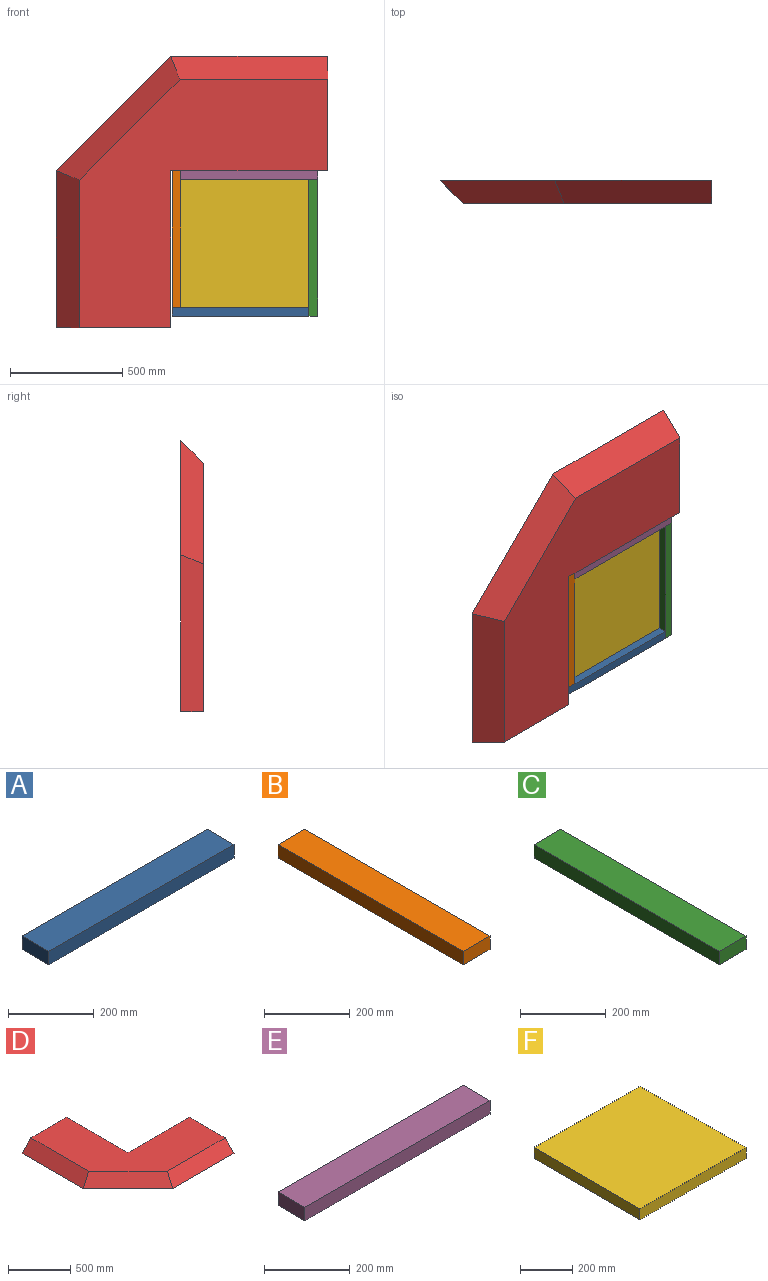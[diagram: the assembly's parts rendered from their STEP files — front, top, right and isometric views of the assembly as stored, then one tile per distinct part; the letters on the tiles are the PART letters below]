
ASSEMBLY  parts=6 mates=5
PART A: 6 faces, bbox 609.6x88.9x38.1 mm
  f0: plane 609.6x38.1mm, normal (0,1,0), area 23225.8mm2, adj f1,f3,f4,f5
  f1: plane 88.9x38.1mm, normal (-1,0,0), area 3387.1mm2, adj f0,f2,f4,f5
  f2: plane 609.6x38.1mm, normal (0,-1,0), area 23225.8mm2, adj f1,f3,f4,f5
  f3: plane 88.9x38.1mm, normal (1,0,0), area 3387.1mm2, adj f0,f2,f4,f5
  f4: plane 609.6x88.9mm, normal (0,0,1), area 54193.4mm2, adj f0,f1,f2,f3
  f5: plane 609.6x88.9mm, normal (0,0,-1), area 54193.4mm2, adj f0,f1,f2,f3
PART B: 6 faces, bbox 88.9x609.6x38.1 mm
  f0: plane 609.6x38.1mm, normal (1,0,0), area 23225.8mm2, adj f1,f3,f4,f5
  f1: plane 88.9x38.1mm, normal (0,1,0), area 3387.1mm2, adj f0,f2,f4,f5
  f2: plane 609.6x38.1mm, normal (-1,0,0), area 23225.8mm2, adj f1,f3,f4,f5
  f3: plane 88.9x38.1mm, normal (0,-1,0), area 3387.1mm2, adj f0,f2,f4,f5
  f4: plane 609.6x88.9mm, normal (0,0,1), area 54193.4mm2, adj f0,f1,f2,f3
  f5: plane 609.6x88.9mm, normal (0,0,-1), area 54193.4mm2, adj f0,f1,f2,f3
PART C: 6 faces, bbox 88.9x609.6x38.1 mm
  f0: plane 88.9x38.1mm, normal (0,1,0), area 3387.1mm2, adj f1,f3,f4,f5
  f1: plane 609.6x38.1mm, normal (-1,0,0), area 23225.8mm2, adj f0,f2,f4,f5
  f2: plane 88.9x38.1mm, normal (0,-1,0), area 3387.1mm2, adj f1,f3,f4,f5
  f3: plane 609.6x38.1mm, normal (1,0,0), area 23225.8mm2, adj f0,f2,f4,f5
  f4: plane 609.6x88.9mm, normal (0,0,1), area 54193.4mm2, adj f0,f1,f2,f3
  f5: plane 609.6x88.9mm, normal (0,0,-1), area 54193.4mm2, adj f0,f1,f2,f3
PART D: 9 faces, bbox 1206.5x1206.5x101.6 mm
  f0: plane 508x101.6mm, normal (1,0,0), area 46451.5mm2, adj f1,f4,f5,f6
  f1: plane 698.5x101.6mm, normal (0,1,0), area 70967.6mm2, adj f0,f2,f4,f5
  f2: plane 698.5x101.6mm, normal (1,0,0), area 70967.6mm2, adj f1,f3,f4,f5
  f3: plane 508x101.6mm, normal (0,1,0), area 46451.5mm2, adj f2,f4,f5,f8
  f4: plane 1104.9x1104.9mm, normal (0,0,1), area 632332.8mm2, adj f0,f1,f2,f3,f6,f7,f8
  f5: plane 1206.5x1206.5mm, normal (0,0,-1), area 838708mm2, adj f0,f1,f2,f3,f6,f7,f8
  f6: plane 698.5x101.6mm, normal (0,-0.71,0.71), area 97339.9mm2, adj f0,f4,f5,f7
  f7: plane 550.08x550.08mm, normal (-0.5,-0.5,0.71), area 97178.8mm2, adj f4,f5,f6,f8
  f8: plane 698.5x101.6mm, normal (-0.71,0,0.71), area 97339.9mm2, adj f3,f4,f5,f7
PART E: 6 faces, bbox 609.6x88.9x38.1 mm
  f0: plane 609.6x38.1mm, normal (0,-1,0), area 23225.8mm2, adj f1,f3,f4,f5
  f1: plane 88.9x38.1mm, normal (1,0,0), area 3387.1mm2, adj f0,f2,f4,f5
  f2: plane 609.6x38.1mm, normal (0,1,0), area 23225.8mm2, adj f1,f3,f4,f5
  f3: plane 88.9x38.1mm, normal (-1,0,0), area 3387.1mm2, adj f0,f2,f4,f5
  f4: plane 609.6x88.9mm, normal (0,0,1), area 54193.4mm2, adj f0,f1,f2,f3
  f5: plane 609.6x88.9mm, normal (0,0,-1), area 54193.4mm2, adj f0,f1,f2,f3
PART F: 6 faces, bbox 571.5x571.5x50.8 mm
  f0: plane 571.5x50.8mm, normal (1,0,0), area 29032.2mm2, adj f1,f3,f4,f5
  f1: plane 571.5x50.8mm, normal (0,1,0), area 29032.2mm2, adj f0,f2,f4,f5
  f2: plane 571.5x50.8mm, normal (-1,0,0), area 29032.2mm2, adj f1,f3,f4,f5
  f3: plane 571.5x50.8mm, normal (0,-1,0), area 29032.2mm2, adj f0,f2,f4,f5
  f4: plane 571.5x571.5mm, normal (0,0,1), area 326612.2mm2, adj f0,f1,f2,f3
  f5: plane 571.5x571.5mm, normal (0,0,-1), area 326612.2mm2, adj f0,f1,f2,f3
PLACE A t=(112.52,473.97,-773.23)mm
PLACE B rot(axis=(0.58,-0.58,-0.58),120deg) t=(-274.92,-156.75,-529.95)mm
PLACE C rot(axis=(0.58,-0.58,-0.58),120deg) t=(334.68,452.85,-479.15)mm
PLACE D rot(axis=(0.58,0.58,-0.58),120deg) t=(-25.3,275.14,-551.07)mm
PLACE E t=(61.72,-135.63,-163.63)mm
PLACE F rot(axis=(0,-0.71,0.71),180deg) t=(-1043.4,268.79,-516.31)mm
MATE fastened D.f2 <-> E.f4  axis (0,0,-1) through (29.88,224.34,-125.53)mm
MATE fastened B.f3 <-> A.f4  axis (0,0,-1) through (-293.97,224.34,-735.13)mm
MATE fastened A.f3 <-> C.f4  axis (1,0,0) through (296.58,224.34,-754.18)mm
MATE fastened F.f0 <-> B.f5  axis (-1,0,0) through (-274.92,268.79,-735.13)mm
MATE fastened C.f0 <-> E.f5  axis (0,0,1) through (315.63,224.34,-163.63)mm
